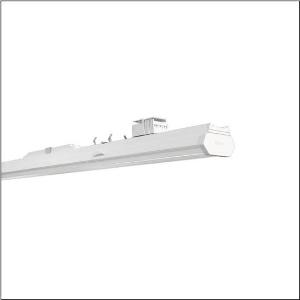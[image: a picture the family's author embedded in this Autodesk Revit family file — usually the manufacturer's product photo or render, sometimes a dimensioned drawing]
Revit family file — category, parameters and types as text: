
# Revit family: licross_r__11_protected_mo_51td1bmn49xg_0ef7
name_source: partatom
category: Lighting Fixtures
units: mm (PartAtom-declared; Revit-internal decimal feet)

## family parameters
Cut with Voids When Loaded = No
Host = Face
Light Source = No
Part Type = Normal
Room Calculation Point = No
Round Connector Dimension = Use Diameter
Shared = No

## types (1)
- --- (1 x LED, 9410 lm, 55.3 W, 4000K)
    Apparent Load = 55 VA
    CIE Flux Codes = 54 82 95 97 100
    Color Rendering = 80
    Color Temperature = 4000K
    Default Elevation = 1800 mm
    Description = Licross® 11 Protected MO, luminaire insert, of sheet steel, galvanised, coil coated, white, length: 1.500mm, width: 90mm, height: 101mm, LED rated luminous flux: 9.420lm, light colour: 840, control gear: ON/OFF Multilumen, with plug, 3-pole, with phase selection, mains connection: 220..240V, AC, 50/60Hz, rated input power: 55W, halogen-free wiring, primary optical cover: cover, of PMMA, light emission: direct distribution, primary light characteristic: symmetric, protection rating (complete): IP54, insulation class (complete): insulation class I (protective earthing), certification: CE, ENEC, VDE, UKCA, protection symbol: D if used in an environment with non-conductive dust loads with corresponding accessories, impact resistance: IK06, permissible ambient temperature for indoor applications: -35..+40°C, corresponds to IFS (International Featured Standards) requirements for safety and quality in the food industry, reducing of maximum allowable ambient temperature of 5°C with ceiling mounting, LABS conformity tested according to VDMA 24364:2018-05, packaging unit: 1 piece
    Height = 92 mm
    Lamp = 1 x LED
    Lamp Light Flux = 9410 lm
    Lamp Power = 55.3 W
    Lamp count = 1
    Length = 1500 mm
    Luminous efficacy = 170 lm/W
    Manufacturer = Siteco
    ModVariant = No
    Model = 51TD1BMN49XG
    Mounting Place = Ceiling
    Mounting Type = Pendant
    Number of Poles = 1
    OnlyDefault = Yes
    Power Factor = 1
    Product Name = Licross® 11 Protected MO
    Product group = luminaire insert
    ProductGroupID = 901
    Protection Class = Protection class I
    Protection Degree = IP 54
    RLX_Detail_Level = 1
    RLX_Emergency_Light_Flux = 0 lm
    RLX_Emergency_Type = 0
    RLX_Emergency_Type_DB = No
    RlxData = <blob elided: 21981 chars, md5=9644fe0e>
    Socket = socket
    Standby Power = 0 W
    System Light Flux = 9410 lm
    System Power = 55 W
    Type Comments = factory setting: luminous flux: 100 % | (A | C | E) | 126 mA
    Type Image = l_1256145.jpg
    URL = http://relux.com
    VarID = @adj_055385
    Voltage = 0 V
    Weight = 0.00 kg
    Width = 88 mm

## geometry (parser evidence)
native form markers: Blend x4, Sweep x10
no freeform markers — native parametric forms only
